# Revit family: PANZERI_BELLA_WALL_RECESSED_LIGHT
name_source: partatom
category: Lighting Fixtures
revit_build: Autodesk Revit 2018 (Build: 20190510_1515(x64)
units: mm (PartAtom-declared; Revit-internal decimal feet)

## family parameters
Cut with Voids When Loaded = No
Host = Face
Light Source = No
OmniClass Number = 23.80.70.00
OmniClass Title = Lighting
Part Type = Normal
Room Calculation Point = Yes
Round Connector Dimension = Use Diameter
Shared = No

## types (1)
- Recessed_Black
    ACCESSORIES = DRIVER: integrated included
    AVAILABLE FINISHES = Structure: white, black, bronze, mat brass or titanium. CUSTOM finishes available only on request.
    Apparent Load = 0 VA
    BIM BADGE = https://bim.archiproducts.com
    COLLECTION = BELLA
    COLOR RENDERING INDEX = Ra>90
    DEPTH = 90 mm
    DESIGNER = Enzo Panzeri
    DIAMETER = 101 mm
    Default Elevation = 1219 mm
    Description = Lighting fixture for wall semi-built-in installation for interiors, with swivelling light beam. Push-button to adjust luminosity according to 5 levels of visual comfort.
    ENERGY EFFICIENCY CLASS = N/D
    FREQUENCY = 0 Hz
    FREQUENCY RANGE = 50/60Hz
    HEIGHT = 159 mm
    INSTALLATION INSTRUCTIONS = https://panzeri.it
    IP RATING = IP20
    LAMP MATERIAL = PANZERI_POLYCARBONATE_OPALINE_SCREEN_Light_on
    LIGHTING SPECIFICATION = LED 5W | 2700K | Ra>90 | 388lm | 220-240V AC | dimmable (Step DIM)
    Lamp = LED
    Light Source Symbol Size = 300 mm
    MATERIAL DESCRIPTION = Pickled sheet metal fixing disk in white polyacrylic paint. Pickled sheet metal wall plate in polyacrylic paint. Turned brass joints in polyacrylic paint. Die-cast aluminium structure in polyacrylic paint. Die-cast aluminium head rotating on three axes in polyacrylic paint. Modelled acrylic diffuser with mat finish.
Aluminium closing disk in polyacrylic paint. Push-button to adjust luminosity according to 5 levels of visual comfort. Recessed housing for masonry or plasterboard, in pickled sheet metal in polyacrylic paint. Pickled sheet metal brackets for plasterboard fixing.
    Manufacturer = PANZERI
    Model = BELLA WALL
    PACKAGING = 13,0 x 24,0 x 12,0 cm
    POWER SUPPLY = 220-240V AC
    PRODUCT CODE = X05202.011.0509
    PRODUCT SHEET = https://www.archiproducts.com
    STRUCTURE MATERIAL = PANZERI_ALUMINIUM_POLYACRYLIC_PAINT_BLACK_02
    TECHNICAL SHEET = https://panzeri.it
    Type Comments = Swivelling light beam. Indirect light emission / Built-in hole dimension: 95x95mm <3,7x3,7in>
    URL = https://panzeri.it
    USAGE = INDOOR - WALL
    VOLTAGE = 0 V
    WATTAGE = 5 W
    WEIGHT = 0.93 kg
    WIDTH = 90 mm

## geometry (parser evidence)
native form markers: Sweep x12
no freeform markers — native parametric forms only
